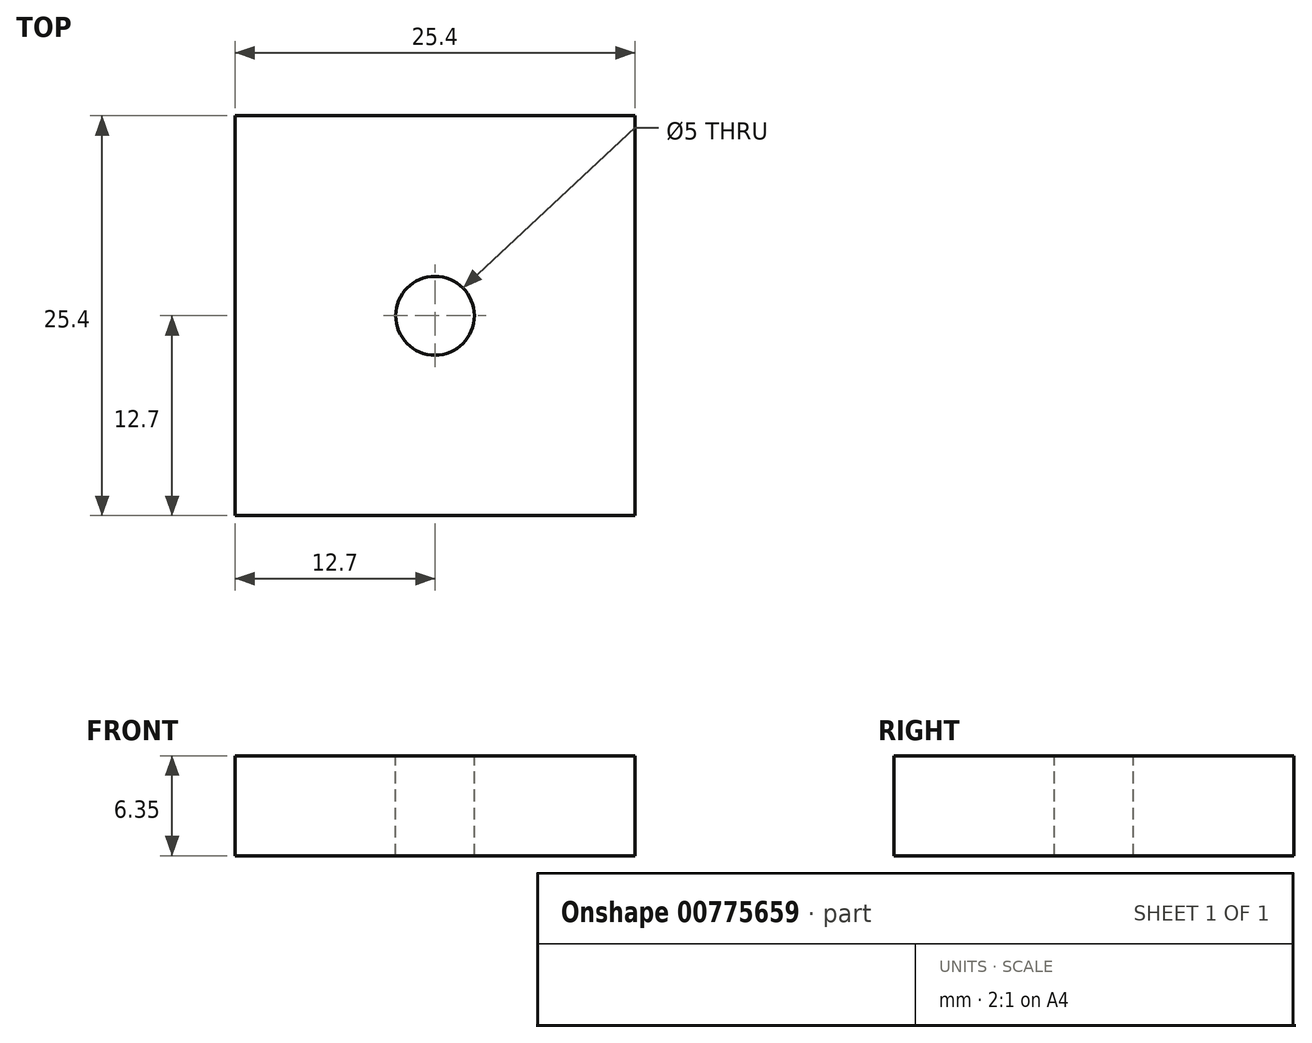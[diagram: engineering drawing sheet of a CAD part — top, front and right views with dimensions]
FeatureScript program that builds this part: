
annotation { "Feature Type Name" : "Feature", "Feature Type Description" : "" }
export const myFeature = defineFeature(function(context is Context, id is Id, definition is map)
    precondition{}
    {
        {
            var Q0;
            Q0=qCreatedBy(makeId("Top.planeOp"),FACE);
            var sketch = newSketch(context, id + "F0", { "sketchPlane" : qUnion([Q0])});
            skLineSegment(sketch, "E0.bottom", {"start": v(12.7, -12.7) * mm, "end": v(-12.7, -12.7) * mm});
            skLineSegment(sketch, "E0.top", {"start": v(12.7, 12.7) * mm, "end": v(-12.7, 12.7) * mm});
            skLineSegment(sketch, "E0.left", {"start": v(12.7, -12.7) * mm, "end": v(12.7, 12.7) * mm});
            skLineSegment(sketch, "E0.right", {"start": v(-12.7, -12.7) * mm, "end": v(-12.7, 12.7) * mm});
            skPoint(sketch, "E0.middle", {"position": v(0, 0) * mm});
            skSolve(sketch);
        }
        {
            var Q0;
            Q0=makeQuery(id+"F0.imprint","IMPRINT",FACE,{"disambiguationData":[TD([[makeQuery(id+"F0.imprint","IMPRINT",EDGE,{"derivedFrom":sQuery(id+"F0.wireOp",EDGE,"E0.bottom")}),-1.0]])]});
            extrude(context, id + "F1", {"entities" : qUnion([Q0]), "depth" : 6.35 * mm, "offsetDistance" : 25 * mm});
        }
        {
            var Q0;
            Q0=makeQuery(id+"F1.opExtrude","CAP_FACE",FACE,{"disambiguationData":[OSD([sQuery(id+"F0.wireOp",EDGE,"E0.bottom"),sQuery(id+"F0.wireOp",EDGE,"E0.top"),sQuery(id+"F0.wireOp",EDGE,"E0.left"),sQuery(id+"F0.wireOp",EDGE,"E0.right")])],"isStart":false});
            var sketch = newSketch(context, id + "F2", { "sketchPlane" : qUnion([Q0])});
            skPoint(sketch, "E1", {"position": v(0, 0) * mm});
            skSolve(sketch);
        }
        {
            var Q0;
            Q0=sQuery(id+"F2.wireOp",VERTEX,"E1");
            var Q1;
            Q1=makeQuery(id+"F1.opExtrude","SWEPT_BODY",BODY,{"disambiguationData":[OSD([sQuery(id+"F0.wireOp",EDGE,"E0.bottom"),sQuery(id+"F0.wireOp",EDGE,"E0.top"),sQuery(id+"F0.wireOp",EDGE,"E0.left"),sQuery(id+"F0.wireOp",EDGE,"E0.right")])]});
            hole(context, id + "F3", {"style" : HoleStyle.SIMPLE, "endStyle" : HoleEndStyle.THROUGH, "standardTappedOrClearance" : lookupTablePath({ "standard" : "ISO", "engagement" : "75%", "pitch" : "1 mm", "size" : "M6", "type" : "Tapped" }), "standardBlindInLast" : lookupTablePath({ "standard" : "ISO", "fit" : "Normal", "engagement" : "75%", "pitch" : "1 mm", "size" : "M6", "type" : "Clearance & tapped" }), "holeDiameter" : 5 * mm, "majorDiameter" : 6 * mm, "showTappedDepth" : true, "isTappedThrough" : true, "tappedDepth" : 12 * mm, "tapClearance" : 3, "locations" : qUnion([Q0]), "scope" : qUnion([Q1])});
        }
    });
